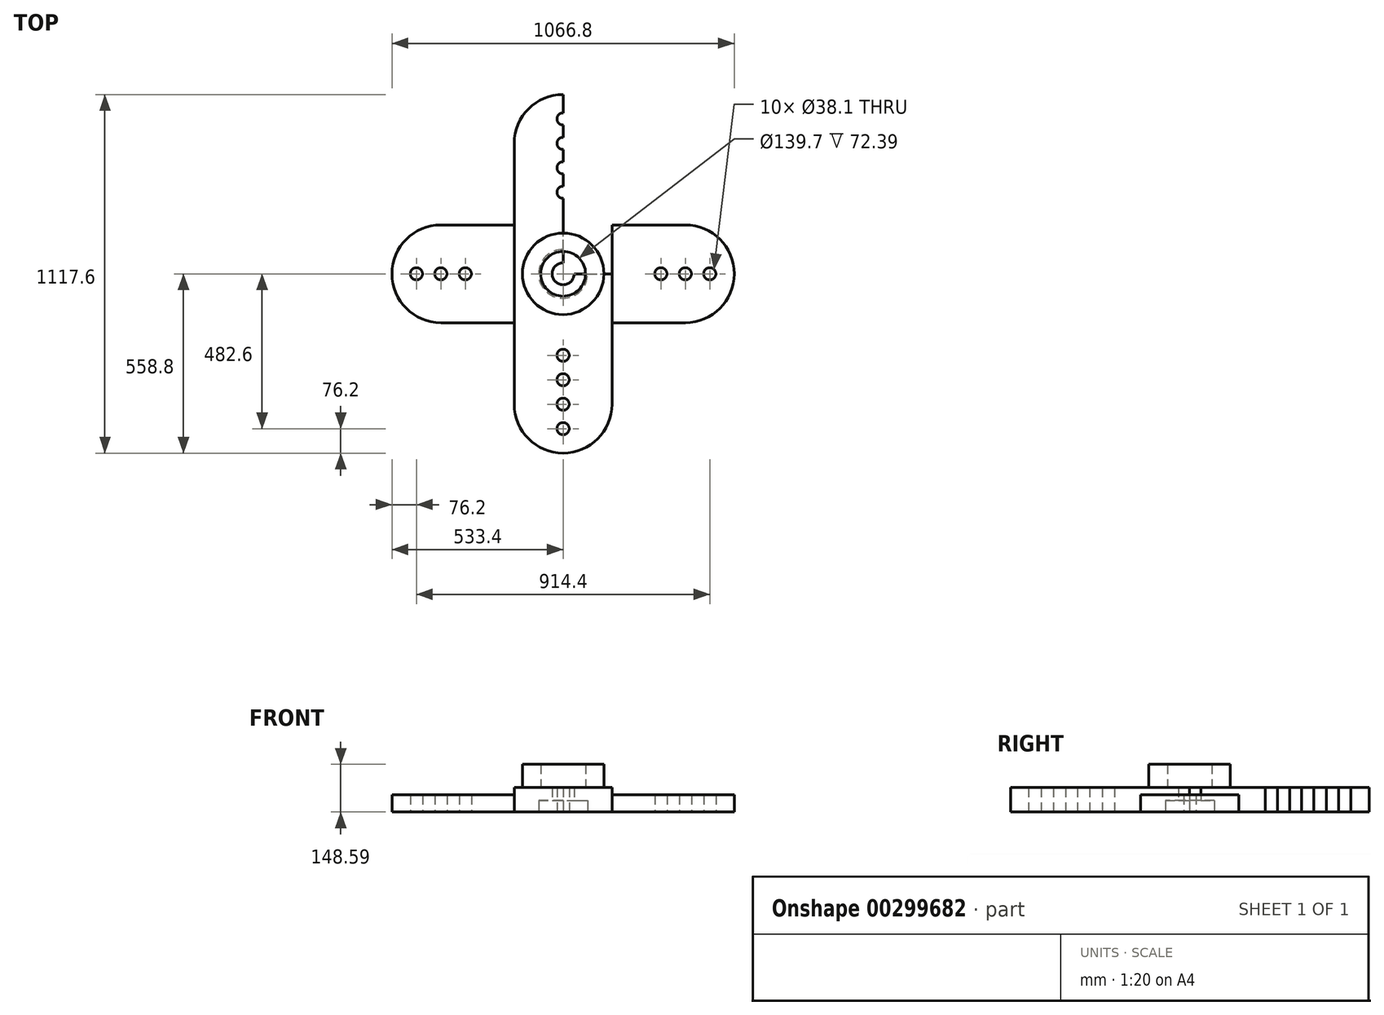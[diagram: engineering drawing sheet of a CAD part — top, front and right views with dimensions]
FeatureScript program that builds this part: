
annotation { "Feature Type Name" : "Feature", "Feature Type Description" : "" }
export const myFeature = defineFeature(function(context is Context, id is Id, definition is map)
    precondition{}
    {
        {
            var Q0;
            Q0=qCreatedBy(makeId("Top.planeOp"),FACE);
            var sketch = newSketch(context, id + "F0", { "sketchPlane" : qUnion([Q0])});
            skLineSegment(sketch, "E0", {"start": v(0, 0) * mm, "end": v(0, 660.4) * mm});
            skLineSegment(sketch, "E1", {"start": v(0, 0) * mm, "end": v(669.1, 0) * mm});
            skArc(sketch, "E2", {"start": v(0, 558.8) * mm, "mid": v(107.76, 514.16) * mm, "end": v(152.4, 406.4) * mm});
            skArc(sketch, "E3", {"start": v(533.4, 0) * mm, "mid": v(488.76, 107.76) * mm, "end": v(381, 152.4) * mm});
            skLineSegment(sketch, "E4", {"start": v(381, 152.4) * mm, "end": v(152.4, 152.4) * mm});
            skLineSegment(sketch, "E5", {"start": v(152.4, 152.4) * mm, "end": v(152.4, 406.4) * mm});
            skCircle(sketch, "E6", {"center": v(0, 406.4) * mm, "radius": 19.05 * mm});
            skCircle(sketch, "E7", {"center": v(0, 482.6) * mm, "radius": 19.05 * mm});
            skCircle(sketch, "E8", {"center": v(0, 330.2) * mm, "radius": 19.05 * mm});
            skCircle(sketch, "E9", {"center": v(0, 254) * mm, "radius": 19.05 * mm});
            skCircle(sketch, "E10", {"center": v(381, 0) * mm, "radius": 19.05 * mm});
            skCircle(sketch, "E11", {"center": v(457.2, 0) * mm, "radius": 19.05 * mm});
            skCircle(sketch, "E12", {"center": v(304.8, 0) * mm, "radius": 19.05 * mm});
            skArc(sketch, "E13.MirrorCS", {"start": v(0, 558.8) * mm, "mid": v(-107.76, 514.16) * mm, "end": v(-152.4, 406.4) * mm});
            skLineSegment(sketch, "E14.MirrorCS", {"start": v(-152.4, 152.4) * mm, "end": v(-152.4, 406.4) * mm});
            skLineSegment(sketch, "E15.MirrorCS", {"start": v(-381, 152.4) * mm, "end": v(-152.4, 152.4) * mm});
            skArc(sketch, "E16.MirrorCS", {"start": v(-533.4, 0) * mm, "mid": v(-488.76, 107.76) * mm, "end": v(-381, 152.4) * mm});
            skCircle(sketch, "E17.MirrorC", {"center": v(-457.2, 0) * mm, "radius": 19.05 * mm});
            skCircle(sketch, "E18.MirrorC", {"center": v(-381, 0) * mm, "radius": 19.05 * mm});
            skCircle(sketch, "E19.MirrorC", {"center": v(-304.8, 0) * mm, "radius": 19.05 * mm});
            skArc(sketch, "E20.MirrorCS", {"start": v(-533.4, 0) * mm, "mid": v(-488.76, -107.76) * mm, "end": v(-381, -152.4) * mm});
            skLineSegment(sketch, "E21.MirrorCS", {"start": v(-381, -152.4) * mm, "end": v(-152.4, -152.4) * mm});
            skLineSegment(sketch, "E22.MirrorCS", {"start": v(-152.4, -152.4) * mm, "end": v(-152.4, -406.4) * mm});
            skArc(sketch, "E23.MirrorCS", {"start": v(0, -558.8) * mm, "mid": v(-107.76, -514.16) * mm, "end": v(-152.4, -406.4) * mm});
            skArc(sketch, "E24.MirrorCS", {"start": v(0, -558.8) * mm, "mid": v(107.76, -514.16) * mm, "end": v(152.4, -406.4) * mm});
            skLineSegment(sketch, "E25.MirrorCS", {"start": v(152.4, -152.4) * mm, "end": v(152.4, -406.4) * mm});
            skLineSegment(sketch, "E26.MirrorCS", {"start": v(381, -152.4) * mm, "end": v(152.4, -152.4) * mm});
            skArc(sketch, "E27.MirrorCS", {"start": v(533.4, 0) * mm, "mid": v(488.76, -107.76) * mm, "end": v(381, -152.4) * mm});
            skCircle(sketch, "E28.MirrorC", {"center": v(0, -254) * mm, "radius": 19.05 * mm});
            skCircle(sketch, "E29.MirrorC", {"center": v(0, -330.2) * mm, "radius": 19.05 * mm});
            skCircle(sketch, "E30.MirrorC", {"center": v(0, -406.4) * mm, "radius": 19.05 * mm});
            skCircle(sketch, "E31.MirrorC", {"center": v(0, -482.6) * mm, "radius": 19.05 * mm});
            skCircle(sketch, "E32", {"center": v(0, 0) * mm, "radius": 34.3 * mm});
            skLineSegment(sketch, "E33", {"start": v(-152.4, 152.4) * mm, "end": v(-152.4, -152.4) * mm});
            skLineSegment(sketch, "E34", {"start": v(152.4, -152.4) * mm, "end": v(152.4, 152.4) * mm});
            skSolve(sketch);
        }
        {
            var Q0;
            {var subQ10=sQuery(id+"F0.wireOp",EDGE,"E13.MirrorCS");Q0=makeQuery(id+"F0.imprint","IMPRINT",FACE,{"disambiguationData":[TD([[makeQuery(id+"F0.imprint","IMPRINT",EDGE,{"derivedFrom":subQ10}),1.0]])]});}
            var Q1;
            {var subQ14=sQuery(id+"F0.wireOp",EDGE,"E2");Q1=makeQuery(id+"F0.imprint","IMPRINT",FACE,{"disambiguationData":[TD([[makeQuery(id+"F0.imprint","IMPRINT",EDGE,{"derivedFrom":subQ14}),-1.0]])]});}
            extrude(context, id + "F1", {"entities" : qUnion([Q0, Q1]), "depth" : 76.2 * mm});
        }
        {
            var Q0;
            Q0=makeQuery(id+"F0.imprint","IMPRINT",FACE,{"disambiguationData":[TD([[makeQuery(id+"F0.imprint","IMPRINT",EDGE,{"derivedFrom":sQuery(id+"F0.wireOp",EDGE,"E15.MirrorCS")}),-1.0]])]});
            var Q1;
            {var subQ0=sQuery(id+"F0.wireOp",EDGE,"E3");Q1=makeQuery(id+"F0.imprint","IMPRINT",FACE,{"disambiguationData":[TD([[makeQuery(id+"F0.imprint","IMPRINT",EDGE,{"derivedFrom":subQ0}),1.0]])]});}
            var Q2;
            {var subQ13=sQuery(id+"F0.wireOp",EDGE,"E26.MirrorCS");Q2=makeQuery(id+"F0.imprint","IMPRINT",FACE,{"disambiguationData":[TD([[makeQuery(id+"F0.imprint","IMPRINT",EDGE,{"derivedFrom":subQ13}),-1.0]])]});}
            extrude(context, id + "F2", {"entities" : qUnion([Q0, Q1, Q2]), "operationType" : NewBodyOperationType.ADD, "depth" : 53.34 * mm});
        }
        {
            var Q0;
            Q0=makeQuery(id+"F1.opExtrude","CAP_FACE",FACE,{"disambiguationData":[OSD([sQuery(id+"F0.wireOp",EDGE,"E2"),sQuery(id+"F0.wireOp",EDGE,"E5"),sQuery(id+"F0.wireOp",EDGE,"E6"),sQuery(id+"F0.wireOp",EDGE,"E7"),sQuery(id+"F0.wireOp",EDGE,"E8"),sQuery(id+"F0.wireOp",EDGE,"E9"),sQuery(id+"F0.wireOp",EDGE,"E13.MirrorCS"),sQuery(id+"F0.wireOp",EDGE,"E14.MirrorCS"),sQuery(id+"F0.wireOp",EDGE,"E22.MirrorCS"),sQuery(id+"F0.wireOp",EDGE,"E23.MirrorCS"),sQuery(id+"F0.wireOp",EDGE,"E24.MirrorCS"),sQuery(id+"F0.wireOp",EDGE,"E25.MirrorCS"),sQuery(id+"F0.wireOp",EDGE,"E28.MirrorC"),sQuery(id+"F0.wireOp",EDGE,"E29.MirrorC"),sQuery(id+"F0.wireOp",EDGE,"E30.MirrorC"),sQuery(id+"F0.wireOp",EDGE,"E31.MirrorC"),sQuery(id+"F0.wireOp",EDGE,"E32"),sQuery(id+"F0.wireOp",EDGE,"E33"),sQuery(id+"F0.wireOp",EDGE,"E34")])],"isStart":false});
            var sketch = newSketch(context, id + "F3", { "sketchPlane" : qUnion([Q0])});
            skCircle(sketch, "E35", {"center": v(0, 0) * mm, "radius": 127 * mm});
            skCircle(sketch, "E36", {"center": v(0, 0) * mm, "radius": 69.85 * mm});
            skSolve(sketch);
        }
        {
            var Q0;
            Q0 = qSketchRegion(id + "F3", true);
            extrude(context, id + "F4", {"entities" : qUnion([Q0]), "operationType" : NewBodyOperationType.ADD, "depth" : 72.39 * mm});
        }
        {
            var Q0;
            {var subQ10=sQuery(id+"F0.wireOp",EDGE,"E13.MirrorCS");Q0=makeQuery(id+"F0.imprint","IMPRINT",FACE,{"disambiguationData":[TD([[makeQuery(id+"F0.imprint","IMPRINT",EDGE,{"derivedFrom":subQ10}),1.0]])]});}
            var sketch = newSketch(context, id + "F5", { "sketchPlane" : qUnion([Q0])});
            skCircle(sketch, "E37", {"center": v(0, 0) * mm, "radius": 76.2 * mm});
            skSolve(sketch);
        }
        {
            var Q0;
            Q0 = qSketchRegion(id + "F5", true);
            extrude(context, id + "F6", {"entities" : qUnion([Q0]), "operationType" : NewBodyOperationType.REMOVE, "depth" : 35.56 * mm});
        }
    });
